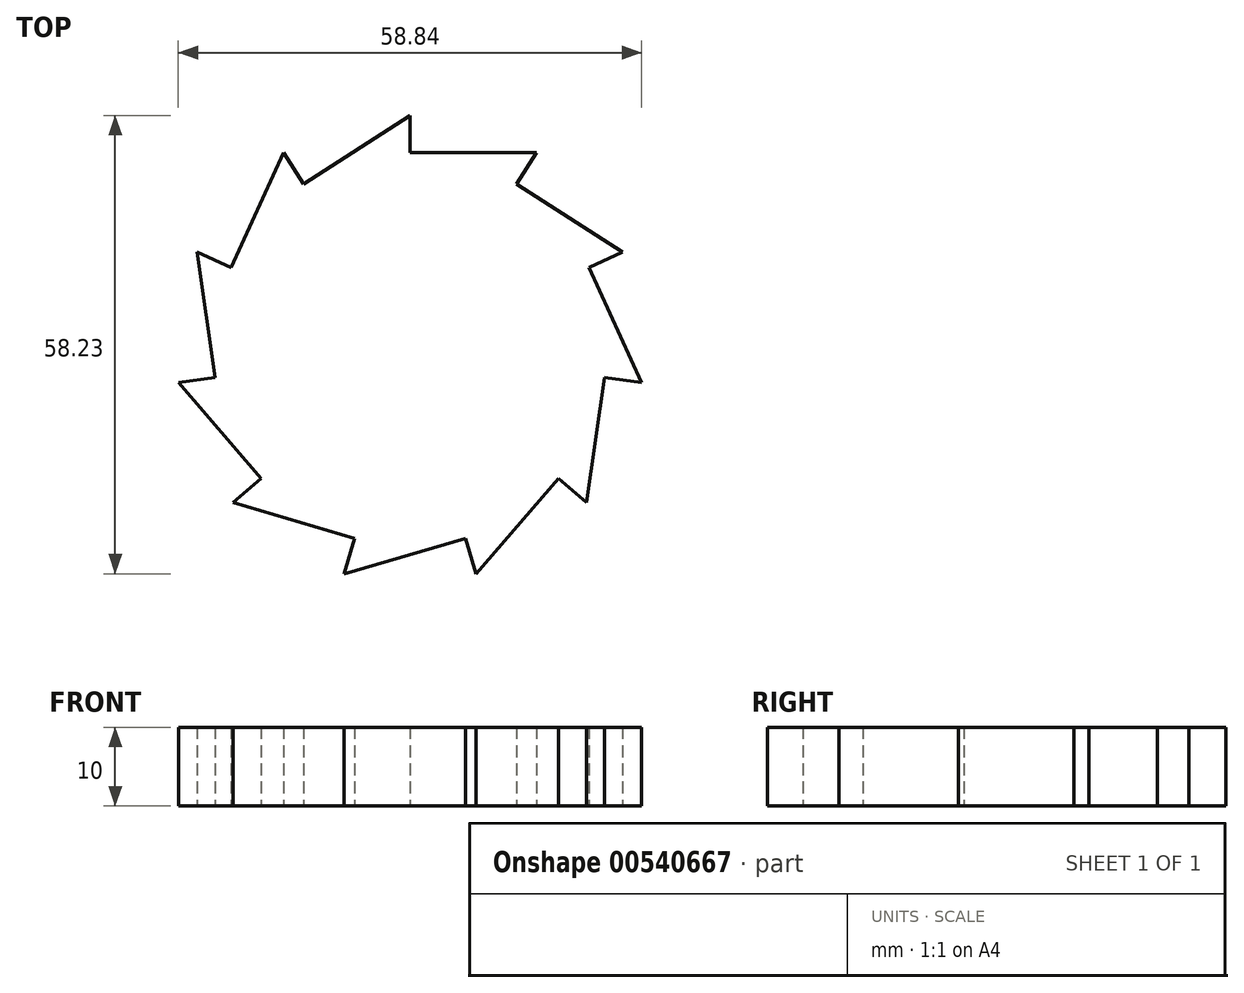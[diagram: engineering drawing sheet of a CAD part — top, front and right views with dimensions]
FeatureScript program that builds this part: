
annotation { "Feature Type Name" : "Feature", "Feature Type Description" : "" }
export const myFeature = defineFeature(function(context is Context, id is Id, definition is map)
    precondition{}
    {
        {
            var Q0;
            Q0=qCreatedBy(makeId("Top.planeOp"),FACE);
            var sketch = newSketch(context, id + "F0", { "sketchPlane" : qUnion([Q0])});
            skCircle(sketch, "E0", {"center": v(0, 0) * mm, "radius": 30 * mm});
            skLineSegment(sketch, "E1", {"start": v(0, 30) * mm, "end": v(0, 25) * mm});
            skLineSegment(sketch, "E2", {"start": v(0, 25) * mm, "end": v(16.58, 25) * mm});
            skLineSegment(sketch, "E3.1.0", {"start": v(-13.52, 21.03) * mm, "end": v(0.43, 30) * mm});
            skLineSegment(sketch, "E3.1.1", {"start": v(-16.22, 25.24) * mm, "end": v(-13.52, 21.03) * mm});
            skLineSegment(sketch, "E3.2.0", {"start": v(-22.74, 10.39) * mm, "end": v(-15.85, 25.47) * mm});
            skLineSegment(sketch, "E3.2.1", {"start": v(-27.29, 12.46) * mm, "end": v(-22.74, 10.39) * mm});
            skLineSegment(sketch, "E4.1.3.0", {"start": v(-24.75, -3.56) * mm, "end": v(-27.1, 12.86) * mm});
            skLineSegment(sketch, "E4.3.3.0", {"start": v(-29.7, -4.27) * mm, "end": v(-24.75, -3.56) * mm});
            skLineSegment(sketch, "E4.1.4.0", {"start": v(-18.9, -16.37) * mm, "end": v(-29.75, -3.84) * mm});
            skLineSegment(sketch, "E4.3.4.0", {"start": v(-22.67, -19.65) * mm, "end": v(-18.9, -16.37) * mm});
            skLineSegment(sketch, "E4.1.5.0", {"start": v(-7.04, -23.99) * mm, "end": v(-22.95, -19.32) * mm});
            skLineSegment(sketch, "E4.3.5.0", {"start": v(-8.45, -28.78) * mm, "end": v(-7.04, -23.99) * mm});
            skLineSegment(sketch, "E4.1.6.0", {"start": v(7.04, -23.99) * mm, "end": v(-8.87, -28.66) * mm});
            skLineSegment(sketch, "E4.3.6.0", {"start": v(8.45, -28.78) * mm, "end": v(7.04, -23.99) * mm});
            skLineSegment(sketch, "E4.1.7.0", {"start": v(18.9, -16.37) * mm, "end": v(8.03, -28.9) * mm});
            skLineSegment(sketch, "E4.3.7.0", {"start": v(22.67, -19.65) * mm, "end": v(18.9, -16.37) * mm});
            skLineSegment(sketch, "E4.1.8.0", {"start": v(24.75, -3.56) * mm, "end": v(22.39, -19.97) * mm});
            skLineSegment(sketch, "E4.3.8.0", {"start": v(29.7, -4.27) * mm, "end": v(24.75, -3.56) * mm});
            skLineSegment(sketch, "E4.1.9.0", {"start": v(22.74, 10.39) * mm, "end": v(29.63, -4.7) * mm});
            skLineSegment(sketch, "E4.3.9.0", {"start": v(27.29, 12.46) * mm, "end": v(22.74, 10.39) * mm});
            skLineSegment(sketch, "E5.1.10.0", {"start": v(13.52, 21.03) * mm, "end": v(27.47, 12.07) * mm});
            skLineSegment(sketch, "E5.3.10.0", {"start": v(16.22, 25.24) * mm, "end": v(13.52, 21.03) * mm});
            skSolve(sketch);
        }
        {
            var Q0;
            {var subQ28=sQuery(id+"F0.wireOp",EDGE,"E2");var subQ29=sQuery(id+"F0.wireOp",EDGE,"E1");var subQ30=makeQuery(id+"F0.imprint","INTERSECT",VERTEX,{"derivedFrom":[subQ29,subQ28]});Q0=makeQuery(id+"F0.imprint","IMPRINT",FACE,{"disambiguationData":[TD([[makeQuery(id+"F0.imprint","IMPRINT",EDGE,{"disambiguationData":[TD([[subQ30,1.0]])],"derivedFrom":subQ29}),-1.0]])]});}
            extrude(context, id + "F1", {"entities" : qUnion([Q0]), "depth" : 10 * mm, "offsetDistance" : 25 * mm});
        }
    });
